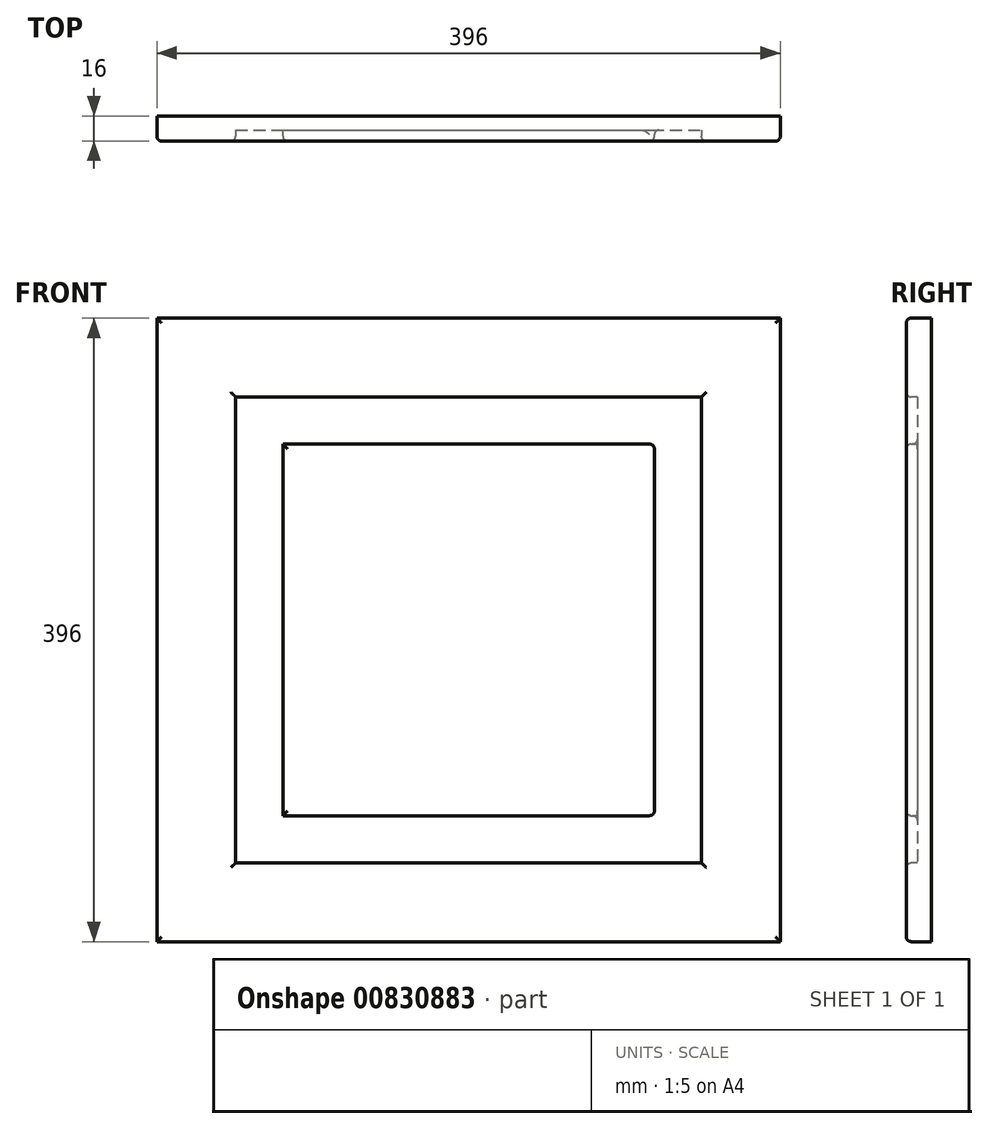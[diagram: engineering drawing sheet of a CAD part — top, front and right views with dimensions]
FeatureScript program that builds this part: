
annotation { "Feature Type Name" : "Feature", "Feature Type Description" : "" }
export const myFeature = defineFeature(function(context is Context, id is Id, definition is map)
    precondition{}
    {
        {
            var Q0;
            Q0=qCreatedBy(makeId("Front.planeOp"),FACE);
            var sketch = newSketch(context, id + "F0", { "sketchPlane" : qUnion([Q0])});
            skLineSegment(sketch, "E0.bottom", {"start": v(0, 0) * mm, "end": v(44.66, 0) * mm});
            skLineSegment(sketch, "E0.top", {"start": v(0, 33.8) * mm, "end": v(44.66, 33.8) * mm});
            skLineSegment(sketch, "E0.left", {"start": v(0, 0) * mm, "end": v(0, 33.8) * mm});
            skLineSegment(sketch, "E0.right", {"start": v(44.66, 0) * mm, "end": v(44.66, 33.8) * mm});
            skSolve(sketch);
        }
        {
            var Q0;
            Q0=makeQuery(id+"F0.imprint","IMPRINT",FACE,{"disambiguationData":[TD([[makeQuery(id+"F0.imprint","IMPRINT",EDGE,{"derivedFrom":sQuery(id+"F0.wireOp",EDGE,"E0.bottom")}),1.0]])]});
            extrude(context, id + "F1", {"entities" : qUnion([Q0]), "depth" : 16 * mm, "offsetDistance" : 25.4 * mm});
        }
        {
            var Q0;
            Q0=makeQuery(id+"F1.opExtrude","SWEPT_FACE",FACE,{"disambiguationData":[OSD([sQuery(id+"F0.wireOp",EDGE,"E0.bottom")])]});
            extrude(context, id + "F2", {"entities" : qUnion([Q0]), "operationType" : NewBodyOperationType.ADD, "oppositeDirection" : true, "depth" : 796 * mm, "offsetDistance" : 25 * mm});
        }
        {
            var Q0;
            {var subQ0=sQuery(id+"F0.wireOp",EDGE,"E0.left");Q0=makeQuery(id+"F2.boolean.opBoolean","MERGE",FACE,{"derivedFrom":[makeQuery(id+"F1.opExtrude","SWEPT_FACE",FACE,{"disambiguationData":[OSD([subQ0])]}),makeQuery(id+"F2.opExtrude","SWEPT_FACE",FACE,{"disambiguationData":[OSD([sQuery(id+"F0.wireOp",EDGE,"E0.bottom"),subQ0])]})]});}
            extrude(context, id + "F3", {"entities" : qUnion([Q0]), "operationType" : NewBodyOperationType.ADD, "oppositeDirection" : true, "depth" : 196 * mm, "offsetDistance" : 25 * mm});
        }
        {
            var Q0;
            {var subQ0=sQuery(id+"F0.wireOp",EDGE,"E0.left");var subQ1=sQuery(id+"F0.wireOp",EDGE,"E0.bottom");Q0=makeQuery(id+"F3.boolean.opBoolean","MERGE",FACE,{"derivedFrom":[makeQuery(id+"F2.boolean.opBoolean","MERGE",FACE,{"derivedFrom":[makeQuery(id+"F1.opExtrude","CAP_FACE",FACE,{"disambiguationData":[OSD([subQ1,sQuery(id+"F0.wireOp",EDGE,"E0.top"),subQ0,sQuery(id+"F0.wireOp",EDGE,"E0.right")])],"isStart":false}),makeQuery(id+"F2.opExtrude","SWEPT_FACE",FACE,{"disambiguationData":[OSD([subQ1]),TDD([makeQuery(id+"F1.opExtrude","CAP_EDGE",EDGE,{"disambiguationData":[OSD([subQ1])],"isStart":false})])]})]}),makeQuery(id+"F3.opExtrude","SWEPT_FACE",FACE,{"disambiguationData":[OSD([subQ1,subQ0]),TDD([makeQuery(id+"F2.boolean.opBoolean","MERGE",EDGE,{"derivedFrom":[makeQuery(id+"F1.opExtrude","CAP_EDGE",EDGE,{"disambiguationData":[OSD([subQ0])],"isStart":false}),makeQuery(id+"F2.opExtrude","SWEPT_EDGE",EDGE,{"disambiguationData":[OSD([subQ1,subQ0]),TDD([makeQuery(id+"F1.opExtrude","CAP_VERTEX",VERTEX,{"disambiguationData":[OSD([subQ1,subQ0])],"isStart":false})])]})]})])]})]});}
            var sketch = newSketch(context, id + "F4", { "sketchPlane" : qUnion([Q0])});
            skLineSegment(sketch, "E1.bottom", {"start": v(59.7, 646.67) * mm, "end": v(128.66, 646.67) * mm});
            skLineSegment(sketch, "E1.top", {"start": v(59.7, 152.97) * mm, "end": v(128.66, 152.97) * mm});
            skLineSegment(sketch, "E1.left", {"start": v(59.7, 646.67) * mm, "end": v(59.7, 152.97) * mm});
            skLineSegment(sketch, "E1.right", {"start": v(128.66, 646.67) * mm, "end": v(128.66, 152.97) * mm});
            skSolve(sketch);
        }
        {
            var Q0;
            Q0=makeQuery(id+"F4.imprint","IMPRINT",FACE,{"disambiguationData":[TD([[makeQuery(id+"F4.imprint","IMPRINT",EDGE,{"derivedFrom":sQuery(id+"F4.wireOp",EDGE,"E1.bottom")}),-1.0]])]});
            extrude(context, id + "F5", {"entities" : qUnion([Q0]), "operationType" : NewBodyOperationType.REMOVE, "oppositeDirection" : true, "depth" : 7 * mm, "offsetDistance" : 25 * mm});
        }
        {
            var Q0;
            Q0=makeQuery(id+"F5.boolean.opBoolean","COPY",FACE,{"derivedFrom":makeQuery(id+"F5.opExtrude","SWEPT_FACE",FACE,{"disambiguationData":[OSD([sQuery(id+"F4.wireOp",EDGE,"E1.left")])]})});
            extrude(context, id + "F6", {"entities" : qUnion([Q0]), "operationType" : NewBodyOperationType.REMOVE, "oppositeDirection" : true, "depth" : 9.7 * mm, "offsetDistance" : 25 * mm});
        }
        {
            var Q0;
            {var subQ0=sQuery(id+"F4.wireOp",EDGE,"E1.bottom");Q0=makeQuery(id+"F6.boolean.opBoolean","MERGE",FACE,{"derivedFrom":[makeQuery(id+"F5.boolean.opBoolean","COPY",FACE,{"derivedFrom":makeQuery(id+"F5.opExtrude","SWEPT_FACE",FACE,{"disambiguationData":[OSD([subQ0])]})}),makeQuery(id+"F6.opExtrude","SWEPT_FACE",FACE,{"disambiguationData":[OSD([subQ0,sQuery(id+"F4.wireOp",EDGE,"E1.left")])]})]});}
            extrude(context, id + "F7", {"entities" : qUnion([Q0]), "operationType" : NewBodyOperationType.ADD, "oppositeDirection" : true, "depth" : 99.33 * mm, "offsetDistance" : 25 * mm});
        }
        {
            var Q0;
            {var subQ0=sQuery(id+"F4.wireOp",EDGE,"E1.bottom");Q0=makeQuery(id+"F6.boolean.opBoolean","MERGE",FACE,{"derivedFrom":[makeQuery(id+"F5.boolean.opBoolean","COPY",FACE,{"derivedFrom":makeQuery(id+"F5.opExtrude","SWEPT_FACE",FACE,{"disambiguationData":[OSD([subQ0])]})}),makeQuery(id+"F6.opExtrude","SWEPT_FACE",FACE,{"disambiguationData":[OSD([subQ0,sQuery(id+"F4.wireOp",EDGE,"E1.left")])]})]});}
            extrude(context, id + "F8", {"entities" : qUnion([Q0]), "operationType" : NewBodyOperationType.REMOVE, "oppositeDirection" : true, "depth" : 99.33 * mm, "offsetDistance" : 25 * mm});
        }
        {
            var Q0;
            {var subQ0=sQuery(id+"F4.wireOp",EDGE,"E1.right");Q0=makeQuery(id+"F8.boolean.opBoolean","MERGE",FACE,{"derivedFrom":[makeQuery(id+"F5.boolean.opBoolean","COPY",FACE,{"derivedFrom":makeQuery(id+"F5.opExtrude","SWEPT_FACE",FACE,{"disambiguationData":[OSD([subQ0])]})}),makeQuery(id+"F8.opExtrude","SWEPT_FACE",FACE,{"disambiguationData":[OSD([sQuery(id+"F4.wireOp",EDGE,"E1.bottom"),subQ0])]})]});}
            extrude(context, id + "F9", {"entities" : qUnion([Q0]), "operationType" : NewBodyOperationType.REMOVE, "oppositeDirection" : true, "depth" : 17.34 * mm, "offsetDistance" : 25 * mm});
        }
        {
            var Q0;
            {var subQ0=sQuery(id+"F4.wireOp",EDGE,"E1.top");Q0=makeQuery(id+"F9.boolean.opBoolean","MERGE",FACE,{"derivedFrom":[makeQuery(id+"F6.boolean.opBoolean","MERGE",FACE,{"derivedFrom":[makeQuery(id+"F5.boolean.opBoolean","COPY",FACE,{"derivedFrom":makeQuery(id+"F5.opExtrude","SWEPT_FACE",FACE,{"disambiguationData":[OSD([subQ0])]})}),makeQuery(id+"F6.opExtrude","SWEPT_FACE",FACE,{"disambiguationData":[OSD([subQ0,sQuery(id+"F4.wireOp",EDGE,"E1.left")])]})]}),makeQuery(id+"F9.opExtrude","SWEPT_FACE",FACE,{"disambiguationData":[OSD([subQ0,sQuery(id+"F4.wireOp",EDGE,"E1.right")])]})]});}
            extrude(context, id + "F10", {"entities" : qUnion([Q0]), "operationType" : NewBodyOperationType.REMOVE, "oppositeDirection" : true, "depth" : 102.97 * mm, "offsetDistance" : 25 * mm});
        }
        {
            var Q0;
            {var subQ0=sQuery(id+"F4.wireOp",EDGE,"E1.right");var subQ1=sQuery(id+"F4.wireOp",EDGE,"E1.top");var subQ2=sQuery(id+"F4.wireOp",EDGE,"E1.left");var subQ3=sQuery(id+"F4.wireOp",EDGE,"E1.bottom");Q0=makeQuery(id+"F10.boolean.opBoolean","MERGE",FACE,{"derivedFrom":[makeQuery(id+"F9.boolean.opBoolean","MERGE",FACE,{"derivedFrom":[makeQuery(id+"F8.boolean.opBoolean","MERGE",FACE,{"derivedFrom":[makeQuery(id+"F6.boolean.opBoolean","MERGE",FACE,{"derivedFrom":[makeQuery(id+"F5.boolean.opBoolean","COPY",FACE,{"derivedFrom":makeQuery(id+"F5.opExtrude","CAP_FACE",FACE,{"disambiguationData":[OSD([subQ3,subQ1,subQ2,subQ0])],"isStart":false})}),makeQuery(id+"F6.opExtrude","SWEPT_FACE",FACE,{"disambiguationData":[OSD([subQ2]),TDD([makeQuery(id+"F5.boolean.opBoolean","COPY",EDGE,{"derivedFrom":makeQuery(id+"F5.opExtrude","CAP_EDGE",EDGE,{"disambiguationData":[OSD([subQ2])],"isStart":false})})])]})]}),makeQuery(id+"F8.opExtrude","SWEPT_FACE",FACE,{"disambiguationData":[OSD([subQ3,subQ2]),TDD([makeQuery(id+"F6.boolean.opBoolean","MERGE",EDGE,{"derivedFrom":[makeQuery(id+"F5.boolean.opBoolean","COPY",EDGE,{"derivedFrom":makeQuery(id+"F5.opExtrude","CAP_EDGE",EDGE,{"disambiguationData":[OSD([subQ3])],"isStart":false})}),makeQuery(id+"F6.opExtrude","SWEPT_EDGE",EDGE,{"disambiguationData":[OSD([subQ3,subQ2]),TDD([makeQuery(id+"F5.boolean.opBoolean","COPY",VERTEX,{"derivedFrom":makeQuery(id+"F5.opExtrude","CAP_VERTEX",VERTEX,{"disambiguationData":[OSD([subQ3,subQ2])],"isStart":false})})])]})]})])]})]}),makeQuery(id+"F9.opExtrude","SWEPT_FACE",FACE,{"disambiguationData":[OSD([subQ3,subQ0]),TDD([makeQuery(id+"F8.boolean.opBoolean","MERGE",EDGE,{"derivedFrom":[makeQuery(id+"F5.boolean.opBoolean","COPY",EDGE,{"derivedFrom":makeQuery(id+"F5.opExtrude","CAP_EDGE",EDGE,{"disambiguationData":[OSD([subQ0])],"isStart":false})}),makeQuery(id+"F8.opExtrude","SWEPT_EDGE",EDGE,{"disambiguationData":[OSD([subQ3,subQ0]),TDD([makeQuery(id+"F5.boolean.opBoolean","COPY",VERTEX,{"derivedFrom":makeQuery(id+"F5.opExtrude","CAP_VERTEX",VERTEX,{"disambiguationData":[OSD([subQ3,subQ0])],"isStart":false})})])]})]})])]})]}),makeQuery(id+"F10.opExtrude","SWEPT_FACE",FACE,{"disambiguationData":[OSD([subQ1,subQ2,subQ0]),TDD([makeQuery(id+"F9.boolean.opBoolean","MERGE",EDGE,{"derivedFrom":[makeQuery(id+"F6.boolean.opBoolean","MERGE",EDGE,{"derivedFrom":[makeQuery(id+"F5.boolean.opBoolean","COPY",EDGE,{"derivedFrom":makeQuery(id+"F5.opExtrude","CAP_EDGE",EDGE,{"disambiguationData":[OSD([subQ1])],"isStart":false})}),makeQuery(id+"F6.opExtrude","SWEPT_EDGE",EDGE,{"disambiguationData":[OSD([subQ1,subQ2]),TDD([makeQuery(id+"F5.boolean.opBoolean","COPY",VERTEX,{"derivedFrom":makeQuery(id+"F5.opExtrude","CAP_VERTEX",VERTEX,{"disambiguationData":[OSD([subQ1,subQ2])],"isStart":false})})])]})]}),makeQuery(id+"F9.opExtrude","SWEPT_EDGE",EDGE,{"disambiguationData":[OSD([subQ1,subQ0]),TDD([makeQuery(id+"F5.boolean.opBoolean","COPY",VERTEX,{"derivedFrom":makeQuery(id+"F5.opExtrude","CAP_VERTEX",VERTEX,{"disambiguationData":[OSD([subQ1,subQ0])],"isStart":false})})])]})]})])]})]});}
            var sketch = newSketch(context, id + "F11", { "sketchPlane" : qUnion([Q0])});
            skLineSegment(sketch, "E2.bottom", {"start": v(74.13, 678.73) * mm, "end": v(109.41, 678.73) * mm});
            skLineSegment(sketch, "E2.top", {"start": v(74.13, 186.63) * mm, "end": v(109.41, 186.63) * mm});
            skLineSegment(sketch, "E2.left", {"start": v(74.13, 678.73) * mm, "end": v(74.13, 186.63) * mm});
            skLineSegment(sketch, "E2.right", {"start": v(109.41, 678.73) * mm, "end": v(109.41, 186.63) * mm});
            skSolve(sketch);
        }
        {
            var Q0;
            Q0=makeQuery(id+"F11.imprint","IMPRINT",FACE,{"disambiguationData":[TD([[makeQuery(id+"F11.imprint","IMPRINT",EDGE,{"derivedFrom":sQuery(id+"F11.wireOp",EDGE,"E2.bottom")}),-1.0]])]});
            extrude(context, id + "F12", {"entities" : qUnion([Q0]), "operationType" : NewBodyOperationType.ADD, "depth" : 7 * mm, "offsetDistance" : 25 * mm});
        }
        {
            var Q0;
            Q0=makeQuery(id+"F12.opExtrude","SWEPT_FACE",FACE,{"disambiguationData":[OSD([sQuery(id+"F11.wireOp",EDGE,"E2.bottom")])]});
            extrude(context, id + "F13", {"entities" : qUnion([Q0]), "operationType" : NewBodyOperationType.ADD, "depth" : 37.27 * mm, "offsetDistance" : 25 * mm});
        }
        {
            var Q0;
            {var subQ0=sQuery(id+"F11.wireOp",EDGE,"E2.right");Q0=makeQuery(id+"F13.boolean.opBoolean","MERGE",FACE,{"derivedFrom":[makeQuery(id+"F12.opExtrude","SWEPT_FACE",FACE,{"disambiguationData":[OSD([subQ0])]}),makeQuery(id+"F13.opExtrude","SWEPT_FACE",FACE,{"disambiguationData":[OSD([sQuery(id+"F11.wireOp",EDGE,"E2.bottom"),subQ0])]})]});}
            extrude(context, id + "F14", {"entities" : qUnion([Q0]), "operationType" : NewBodyOperationType.ADD, "depth" : 6.58 * mm, "offsetDistance" : 25 * mm});
        }
        {
            var Q0;
            {var subQ0=sQuery(id+"F11.wireOp",EDGE,"E2.top");Q0=makeQuery(id+"F14.boolean.opBoolean","MERGE",FACE,{"derivedFrom":[makeQuery(id+"F12.opExtrude","SWEPT_FACE",FACE,{"disambiguationData":[OSD([subQ0])]}),makeQuery(id+"F14.opExtrude","SWEPT_FACE",FACE,{"disambiguationData":[OSD([subQ0,sQuery(id+"F11.wireOp",EDGE,"E2.right")])]})]});}
            extrude(context, id + "F15", {"entities" : qUnion([Q0]), "operationType" : NewBodyOperationType.ADD, "depth" : 106.63 * mm, "offsetDistance" : 25 * mm});
        }
        {
            var Q0;
            {var subQ0=sQuery(id+"F11.wireOp",EDGE,"E2.left");Q0=makeQuery(id+"F15.boolean.opBoolean","MERGE",FACE,{"derivedFrom":[makeQuery(id+"F13.boolean.opBoolean","MERGE",FACE,{"derivedFrom":[makeQuery(id+"F12.opExtrude","SWEPT_FACE",FACE,{"disambiguationData":[OSD([subQ0])]}),makeQuery(id+"F13.opExtrude","SWEPT_FACE",FACE,{"disambiguationData":[OSD([sQuery(id+"F11.wireOp",EDGE,"E2.bottom"),subQ0])]})]}),makeQuery(id+"F15.opExtrude","SWEPT_FACE",FACE,{"disambiguationData":[OSD([sQuery(id+"F11.wireOp",EDGE,"E2.top"),subQ0])]})]});}
            extrude(context, id + "F16", {"entities" : qUnion([Q0]), "operationType" : NewBodyOperationType.REMOVE, "oppositeDirection" : true, "depth" : 5.87 * mm, "offsetDistance" : 25 * mm});
        }
        {
            var Q0;
            Q0=makeQuery(id+"F3.opExtrude","CAP_FACE",FACE,{"disambiguationData":[OSD([sQuery(id+"F0.wireOp",EDGE,"E0.bottom"),sQuery(id+"F0.wireOp",EDGE,"E0.left")])],"isStart":false});
            extrude(context, id + "F17", {"entities" : qUnion([Q0]), "operationType" : NewBodyOperationType.ADD, "depth" : 200 * mm, "offsetDistance" : 25 * mm});
        }
        {
            var Q0;
            {var subQ0=sQuery(id+"F4.wireOp",EDGE,"E1.right");Q0=makeQuery(id+"F10.boolean.opBoolean","MERGE",FACE,{"derivedFrom":[makeQuery(id+"F9.boolean.opBoolean","COPY",FACE,{"derivedFrom":makeQuery(id+"F9.opExtrude","CAP_FACE",FACE,{"disambiguationData":[OSD([sQuery(id+"F4.wireOp",EDGE,"E1.bottom"),subQ0])],"isStart":false})}),makeQuery(id+"F10.opExtrude","SWEPT_FACE",FACE,{"disambiguationData":[OSD([sQuery(id+"F4.wireOp",EDGE,"E1.top"),subQ0])]})]});}
            extrude(context, id + "F18", {"entities" : qUnion([Q0]), "operationType" : NewBodyOperationType.REMOVE, "oppositeDirection" : true, "depth" : 200 * mm, "offsetDistance" : 25 * mm});
        }
        {
            var Q0;
            {var subQ0=sQuery(id+"F11.wireOp",EDGE,"E2.right");var subQ1=sQuery(id+"F11.wireOp",EDGE,"E2.top");Q0=makeQuery(id+"F15.boolean.opBoolean","MERGE",FACE,{"derivedFrom":[makeQuery(id+"F14.opExtrude","CAP_FACE",FACE,{"disambiguationData":[OSD([sQuery(id+"F11.wireOp",EDGE,"E2.bottom"),subQ0])],"isStart":false}),makeQuery(id+"F15.opExtrude","SWEPT_FACE",FACE,{"disambiguationData":[OSD([subQ1,subQ0]),TDD([makeQuery(id+"F14.opExtrude","CAP_EDGE",EDGE,{"disambiguationData":[OSD([subQ1,subQ0])],"isStart":false})])]})]});}
            extrude(context, id + "F19", {"entities" : qUnion([Q0]), "operationType" : NewBodyOperationType.ADD, "depth" : 200 * mm, "offsetDistance" : 25 * mm});
        }
        {
            var Q0;
            {var subQ0=sQuery(id+"F11.wireOp",EDGE,"E2.right");var subQ1=sQuery(id+"F11.wireOp",EDGE,"E2.top");Q0=makeQuery(id+"F19.boolean.opBoolean","MERGE",FACE,{"derivedFrom":[makeQuery(id+"F15.opExtrude","CAP_FACE",FACE,{"disambiguationData":[OSD([subQ1,subQ0])],"isStart":false}),makeQuery(id+"F19.opExtrude","SWEPT_FACE",FACE,{"disambiguationData":[OSD([subQ1,subQ0])]})]});}
            extrude(context, id + "F20", {"entities" : qUnion([Q0]), "operationType" : NewBodyOperationType.REMOVE, "oppositeDirection" : true, "depth" : 600 * mm, "offsetDistance" : 25 * mm});
        }
        {
            var Q0;
            {var subQ0=sQuery(id+"F4.wireOp",EDGE,"E1.right");var subQ1=sQuery(id+"F4.wireOp",EDGE,"E1.top");Q0=makeQuery(id+"F18.boolean.opBoolean","MERGE",FACE,{"derivedFrom":[makeQuery(id+"F10.boolean.opBoolean","COPY",FACE,{"derivedFrom":makeQuery(id+"F10.opExtrude","CAP_FACE",FACE,{"disambiguationData":[OSD([subQ1,sQuery(id+"F4.wireOp",EDGE,"E1.left"),subQ0])],"isStart":false})}),makeQuery(id+"F18.opExtrude","SWEPT_FACE",FACE,{"disambiguationData":[OSD([subQ1,subQ0])]})]});}
            extrude(context, id + "F21", {"entities" : qUnion([Q0]), "operationType" : NewBodyOperationType.ADD, "depth" : 600 * mm, "offsetDistance" : 25 * mm});
        }
        {
            var Q0;
            {var subQ0=sQuery(id+"F0.wireOp",EDGE,"E0.left");var subQ1=sQuery(id+"F0.wireOp",EDGE,"E0.bottom");var subQ2=makeQuery(id+"F1.opExtrude","SWEPT_EDGE",EDGE,{"disambiguationData":[OSD([subQ1,subQ0])]});Q0=makeQuery(id+"F17.boolean.opBoolean","MERGE",FACE,{"derivedFrom":[makeQuery(id+"F3.boolean.opBoolean","MERGE",FACE,{"derivedFrom":[makeQuery(id+"F1.opExtrude","SWEPT_FACE",FACE,{"disambiguationData":[OSD([subQ1])]}),makeQuery(id+"F3.opExtrude","SWEPT_FACE",FACE,{"disambiguationData":[OSD([subQ1,subQ0]),TDD([subQ2])]})]}),makeQuery(id+"F17.opExtrude","SWEPT_FACE",FACE,{"disambiguationData":[OSD([subQ1,subQ0]),TDD([makeQuery(id+"F3.opExtrude","CAP_EDGE",EDGE,{"disambiguationData":[OSD([subQ1,subQ0]),TDD([subQ2])],"isStart":false})])]})]});}
            extrude(context, id + "F22", {"entities" : qUnion([Q0]), "operationType" : NewBodyOperationType.REMOVE, "oppositeDirection" : true, "depth" : 600 * mm, "offsetDistance" : 25 * mm});
        }
        {
            var Q0;
            Q0=makeQuery(id+"F22.boolean.opBoolean","COPY",FACE,{"derivedFrom":makeQuery(id+"F22.opExtrude","CAP_FACE",FACE,{"disambiguationData":[OSD([sQuery(id+"F0.wireOp",EDGE,"E0.bottom"),sQuery(id+"F0.wireOp",EDGE,"E0.left")])],"isStart":false})});
            extrude(context, id + "F23", {"entities" : qUnion([Q0]), "operationType" : NewBodyOperationType.ADD, "depth" : 200 * mm, "offsetDistance" : 25 * mm});
        }
        {
            var Q0;
            Q0=makeQuery(id+"F21.opExtrude","CAP_FACE",FACE,{"disambiguationData":[OSD([sQuery(id+"F4.wireOp",EDGE,"E1.top"),sQuery(id+"F4.wireOp",EDGE,"E1.left"),sQuery(id+"F4.wireOp",EDGE,"E1.right")])],"isStart":false});
            extrude(context, id + "F24", {"entities" : qUnion([Q0]), "operationType" : NewBodyOperationType.REMOVE, "oppositeDirection" : true, "depth" : 200 * mm, "offsetDistance" : 25 * mm});
        }
        {
            var Q0;
            Q0=makeQuery(id+"F20.boolean.opBoolean","COPY",FACE,{"derivedFrom":makeQuery(id+"F20.opExtrude","CAP_FACE",FACE,{"disambiguationData":[OSD([sQuery(id+"F11.wireOp",EDGE,"E2.top"),sQuery(id+"F11.wireOp",EDGE,"E2.right")])],"isStart":false})});
            extrude(context, id + "F25", {"entities" : qUnion([Q0]), "operationType" : NewBodyOperationType.ADD, "depth" : 200 * mm, "offsetDistance" : 25 * mm});
        }
        {
            var Q0;
            {var subQ0=sQuery(id+"F11.wireOp",EDGE,"E2.right");var subQ1=sQuery(id+"F11.wireOp",EDGE,"E2.top");var subQ2=makeQuery(id+"F12.opExtrude","CAP_VERTEX",VERTEX,{"disambiguationData":[OSD([subQ1,subQ0])],"isStart":false});var subQ3=makeQuery(id+"F14.opExtrude","CAP_VERTEX",VERTEX,{"disambiguationData":[OSD([subQ1,subQ0]),TDD([subQ2])],"isStart":false});var subQ4=makeQuery(id+"F14.boolean.opBoolean","MERGE",EDGE,{"derivedFrom":[makeQuery(id+"F12.opExtrude","CAP_EDGE",EDGE,{"disambiguationData":[OSD([subQ1])],"isStart":false}),makeQuery(id+"F14.opExtrude","SWEPT_EDGE",EDGE,{"disambiguationData":[OSD([subQ1,subQ0]),TDD([subQ2])]})]});var subQ5=sQuery(id+"F11.wireOp",EDGE,"E2.bottom");var subQ6=makeQuery(id+"F13.boolean.opBoolean","MERGE",EDGE,{"derivedFrom":[makeQuery(id+"F12.opExtrude","CAP_EDGE",EDGE,{"disambiguationData":[OSD([subQ0])],"isStart":false}),makeQuery(id+"F13.opExtrude","SWEPT_EDGE",EDGE,{"disambiguationData":[OSD([subQ5,subQ0]),TDD([makeQuery(id+"F12.opExtrude","CAP_VERTEX",VERTEX,{"disambiguationData":[OSD([subQ5,subQ0])],"isStart":false})])]})]});Q0=makeQuery(id+"F25.boolean.opBoolean","MERGE",FACE,{"derivedFrom":[makeQuery(id+"F19.boolean.opBoolean","MERGE",FACE,{"derivedFrom":[makeQuery(id+"F15.boolean.opBoolean","MERGE",FACE,{"derivedFrom":[makeQuery(id+"F14.boolean.opBoolean","MERGE",FACE,{"derivedFrom":[makeQuery(id+"F13.boolean.opBoolean","MERGE",FACE,{"derivedFrom":[makeQuery(id+"F12.opExtrude","CAP_FACE",FACE,{"disambiguationData":[OSD([subQ5,subQ1,sQuery(id+"F11.wireOp",EDGE,"E2.left"),subQ0])],"isStart":false}),makeQuery(id+"F13.opExtrude","SWEPT_FACE",FACE,{"disambiguationData":[OSD([subQ5]),TDD([makeQuery(id+"F12.opExtrude","CAP_EDGE",EDGE,{"disambiguationData":[OSD([subQ5])],"isStart":false})])]})]}),makeQuery(id+"F14.opExtrude","SWEPT_FACE",FACE,{"disambiguationData":[OSD([subQ5,subQ0]),TDD([subQ6])]})]}),makeQuery(id+"F15.opExtrude","SWEPT_FACE",FACE,{"disambiguationData":[OSD([subQ1,subQ0]),TDD([subQ4])]})]}),makeQuery(id+"F19.opExtrude","SWEPT_FACE",FACE,{"disambiguationData":[OSD([subQ5,subQ1,subQ0]),TDD([makeQuery(id+"F15.boolean.opBoolean","MERGE",EDGE,{"derivedFrom":[makeQuery(id+"F14.opExtrude","CAP_EDGE",EDGE,{"disambiguationData":[OSD([subQ5,subQ0]),TDD([subQ6])],"isStart":false}),makeQuery(id+"F15.opExtrude","SWEPT_EDGE",EDGE,{"disambiguationData":[OSD([subQ1,subQ0]),TDD([subQ3])]})]})])]})]}),makeQuery(id+"F25.opExtrude","SWEPT_FACE",FACE,{"disambiguationData":[OSD([subQ1,subQ0]),TDD([makeQuery(id+"F20.boolean.opBoolean","COPY",EDGE,{"derivedFrom":makeQuery(id+"F20.opExtrude","CAP_EDGE",EDGE,{"disambiguationData":[OSD([subQ1,subQ0]),TDD([makeQuery(id+"F19.boolean.opBoolean","MERGE",EDGE,{"derivedFrom":[makeQuery(id+"F15.opExtrude","CAP_EDGE",EDGE,{"disambiguationData":[OSD([subQ1,subQ0]),TDD([subQ4])],"isStart":false}),makeQuery(id+"F19.opExtrude","SWEPT_EDGE",EDGE,{"disambiguationData":[OSD([subQ1,subQ0]),TDD([makeQuery(id+"F15.opExtrude","CAP_VERTEX",VERTEX,{"disambiguationData":[OSD([subQ1,subQ0]),TDD([subQ3])],"isStart":false})])]})]})])],"isStart":false})})])]})]});}
            var Q1;
            {var subQ0=sQuery(id+"F0.wireOp",EDGE,"E0.left");var subQ1=sQuery(id+"F0.wireOp",EDGE,"E0.bottom");var subQ2=makeQuery(id+"F1.opExtrude","CAP_VERTEX",VERTEX,{"disambiguationData":[OSD([subQ1,subQ0])],"isStart":false});var subQ3=makeQuery(id+"F1.opExtrude","CAP_EDGE",EDGE,{"disambiguationData":[OSD([subQ1])],"isStart":false});var subQ4=sQuery(id+"F4.wireOp",EDGE,"E1.right");var subQ5=sQuery(id+"F4.wireOp",EDGE,"E1.top");var subQ6=makeQuery(id+"F5.boolean.opBoolean","COPY",VERTEX,{"derivedFrom":makeQuery(id+"F5.opExtrude","CAP_VERTEX",VERTEX,{"disambiguationData":[OSD([subQ5,subQ4])],"isStart":true})});var subQ7=sQuery(id+"F4.wireOp",EDGE,"E1.left");var subQ8=makeQuery(id+"F2.boolean.opBoolean","MERGE",EDGE,{"derivedFrom":[makeQuery(id+"F1.opExtrude","CAP_EDGE",EDGE,{"disambiguationData":[OSD([subQ0])],"isStart":false}),makeQuery(id+"F2.opExtrude","SWEPT_EDGE",EDGE,{"disambiguationData":[OSD([subQ1,subQ0]),TDD([subQ2])]})]});Q1=makeQuery(id+"F23.boolean.opBoolean","MERGE",FACE,{"derivedFrom":[makeQuery(id+"F21.boolean.opBoolean","MERGE",FACE,{"derivedFrom":[makeQuery(id+"F17.boolean.opBoolean","MERGE",FACE,{"derivedFrom":[makeQuery(id+"F3.boolean.opBoolean","MERGE",FACE,{"derivedFrom":[makeQuery(id+"F2.boolean.opBoolean","MERGE",FACE,{"derivedFrom":[makeQuery(id+"F1.opExtrude","CAP_FACE",FACE,{"disambiguationData":[OSD([subQ1,sQuery(id+"F0.wireOp",EDGE,"E0.top"),subQ0,sQuery(id+"F0.wireOp",EDGE,"E0.right")])],"isStart":false}),makeQuery(id+"F2.opExtrude","SWEPT_FACE",FACE,{"disambiguationData":[OSD([subQ1]),TDD([subQ3])]})]}),makeQuery(id+"F3.opExtrude","SWEPT_FACE",FACE,{"disambiguationData":[OSD([subQ1,subQ0]),TDD([subQ8])]})]}),makeQuery(id+"F17.opExtrude","SWEPT_FACE",FACE,{"disambiguationData":[OSD([subQ1,subQ0]),TDD([makeQuery(id+"F3.opExtrude","CAP_EDGE",EDGE,{"disambiguationData":[OSD([subQ1,subQ0]),TDD([subQ8])],"isStart":false})])]})]}),makeQuery(id+"F21.opExtrude","SWEPT_FACE",FACE,{"disambiguationData":[OSD([subQ5,subQ7,subQ4]),TDD([makeQuery(id+"F18.boolean.opBoolean","MERGE",EDGE,{"derivedFrom":[makeQuery(id+"F10.boolean.opBoolean","COPY",EDGE,{"derivedFrom":makeQuery(id+"F10.opExtrude","CAP_EDGE",EDGE,{"disambiguationData":[OSD([subQ5,subQ7,subQ4]),TDD([makeQuery(id+"F9.boolean.opBoolean","MERGE",EDGE,{"derivedFrom":[makeQuery(id+"F6.boolean.opBoolean","MERGE",EDGE,{"derivedFrom":[makeQuery(id+"F5.boolean.opBoolean","COPY",EDGE,{"derivedFrom":makeQuery(id+"F5.opExtrude","CAP_EDGE",EDGE,{"disambiguationData":[OSD([subQ5])],"isStart":true})}),makeQuery(id+"F6.opExtrude","SWEPT_EDGE",EDGE,{"disambiguationData":[OSD([subQ5,subQ7]),TDD([makeQuery(id+"F5.boolean.opBoolean","COPY",VERTEX,{"derivedFrom":makeQuery(id+"F5.opExtrude","CAP_VERTEX",VERTEX,{"disambiguationData":[OSD([subQ5,subQ7])],"isStart":true})})])]})]}),makeQuery(id+"F9.opExtrude","SWEPT_EDGE",EDGE,{"disambiguationData":[OSD([subQ5,subQ4]),TDD([subQ6])]})]})])],"isStart":false})}),makeQuery(id+"F18.opExtrude","SWEPT_EDGE",EDGE,{"disambiguationData":[OSD([subQ5,subQ4]),TDD([makeQuery(id+"F10.boolean.opBoolean","COPY",VERTEX,{"derivedFrom":makeQuery(id+"F10.opExtrude","CAP_VERTEX",VERTEX,{"disambiguationData":[OSD([subQ5,subQ4]),TDD([makeQuery(id+"F9.boolean.opBoolean","COPY",VERTEX,{"derivedFrom":makeQuery(id+"F9.opExtrude","CAP_VERTEX",VERTEX,{"disambiguationData":[OSD([subQ5,subQ4]),TDD([subQ6])],"isStart":false})})])],"isStart":false})})])]})]})])]})]}),makeQuery(id+"F23.opExtrude","SWEPT_FACE",FACE,{"disambiguationData":[OSD([subQ1,subQ0]),TDD([makeQuery(id+"F22.boolean.opBoolean","COPY",EDGE,{"derivedFrom":makeQuery(id+"F22.opExtrude","CAP_EDGE",EDGE,{"disambiguationData":[OSD([subQ1,subQ0]),TDD([makeQuery(id+"F17.boolean.opBoolean","MERGE",EDGE,{"derivedFrom":[makeQuery(id+"F3.boolean.opBoolean","MERGE",EDGE,{"derivedFrom":[subQ3,makeQuery(id+"F3.opExtrude","SWEPT_EDGE",EDGE,{"disambiguationData":[OSD([subQ1,subQ0]),TDD([subQ2])]})]}),makeQuery(id+"F17.opExtrude","SWEPT_EDGE",EDGE,{"disambiguationData":[OSD([subQ1,subQ0]),TDD([makeQuery(id+"F3.opExtrude","CAP_VERTEX",VERTEX,{"disambiguationData":[OSD([subQ1,subQ0]),TDD([subQ2])],"isStart":false})])]})]})])],"isStart":false})})])]})]});}
            fillet(context, id + "F26", {"entities" : qUnion([Q0, Q1]), "radius" : 3 * mm, "tangentPropagation" : true, "allowEdgeOverflow" : false});
        }
    });
